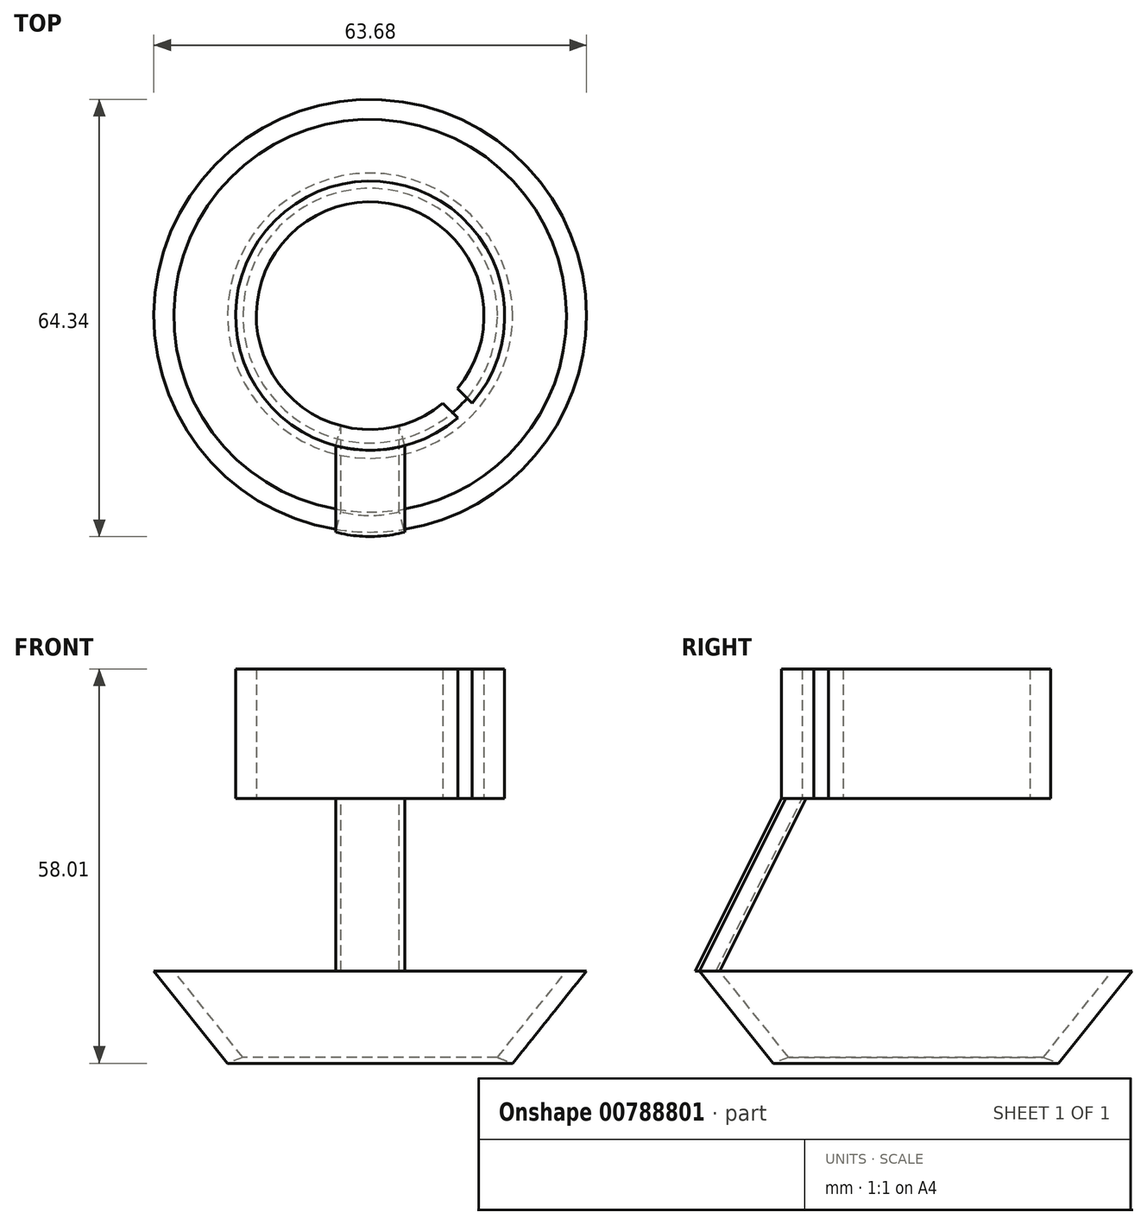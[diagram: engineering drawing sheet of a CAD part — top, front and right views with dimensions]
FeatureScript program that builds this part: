
annotation { "Feature Type Name" : "Feature", "Feature Type Description" : "" }
export const myFeature = defineFeature(function(context is Context, id is Id, definition is map)
    precondition{}
    {
        {
            var Q0;
            Q0=qCreatedBy(makeId("Top.planeOp"),FACE);
            var sketch = newSketch(context, id + "F0", { "sketchPlane" : qUnion([Q0])});
            skArc(sketch, "E0", {"start": v(12.87, -10.72) * mm, "mid": v(-11.84, 11.84) * mm, "end": v(10.72, -12.87) * mm});
            skArc(sketch, "E1.0", {"start": v(15.04, -12.88) * mm, "mid": v(-14, 14) * mm, "end": v(12.88, -15.04) * mm});
            skLineSegment(sketch, "E2", {"start": v(0, 0) * mm, "end": v(19.8, 0) * mm, "construction": true});
            skLineSegment(sketch, "E3", {"start": v(0, 0) * mm, "end": v(14.47, -14.47) * mm, "construction": true});
            skLineSegment(sketch, "E4.0", {"start": v(10.72, -12.87) * mm, "end": v(12.88, -15.04) * mm});
            skLineSegment(sketch, "E5.trimOffspring", {"start": v(12.87, -10.72) * mm, "end": v(15.04, -12.88) * mm});
            skSolve(sketch);
        }
        {
            var Q0;
            Q0=qSketchRegion(id+"F0",true);
            extrude(context, id + "F1", {"entities" : qUnion([Q0]), "depth" : 19.05 * mm, "offsetDistance" : 25.4 * mm});
        }
        {
            var Q0;
            Q0=makeQuery(id+"F1.opExtrude","CAP_FACE",FACE,{"disambiguationData":[OSD([sQuery(id+"F0.wireOp",EDGE,"E0"),sQuery(id+"F0.wireOp",EDGE,"E1.0")])],"isStart":true});
            var sketch = newSketch(context, id + "F2", { "sketchPlane" : qUnion([Q0])});
            skLineSegment(sketch, "E6", {"start": v(0, 0) * mm, "end": v(0, 22.55) * mm, "construction": true});
            skLineSegment(sketch, "E7", {"start": v(0, 22.55) * mm, "end": v(5.08, 22.55) * mm, "construction": true});
            skLineSegment(sketch, "E8", {"start": v(0, 22.55) * mm, "end": v(-5.08, 22.55) * mm, "construction": true});
            skLineSegment(sketch, "E9", {"start": v(-5.08, 22.55) * mm, "end": v(-5.08, 15.96) * mm, "construction": true});
            skLineSegment(sketch, "E10", {"start": v(5.08, 22.55) * mm, "end": v(5.08, 15.96) * mm, "construction": true});
            skLineSegment(sketch, "E11", {"start": v(-5.08, 19.14) * mm, "end": v(-4.3, 16.2) * mm});
            skLineSegment(sketch, "E12", {"start": v(5.08, 19.14) * mm, "end": v(4.3, 16.2) * mm});
            skArc(sketch, "E13.0", {"start": v(5.08, 19.14) * mm, "mid": v(0, -19.8) * mm, "end": v(-5.08, 19.14) * mm});
            skArc(sketch, "E14.0", {"start": v(5.08, 15.96) * mm, "mid": v(0, -16.75) * mm, "end": v(-5.08, 15.96) * mm});
            skPoint(sketch, "E15", {"position": v(-19.8, 0) * mm});
            skPoint(sketch, "E16", {"position": v(0, 19.8) * mm});
            skSolve(sketch);
        }
        {
            var Q0;
            Q0=qCreatedBy(makeId("Right.planeOp"),FACE);
            var sketch = newSketch(context, id + "F3", { "sketchPlane" : qUnion([Q0])});
            skPoint(sketch, "E17.0", {"position": v(-19.8, 0) * mm});
            skLineSegment(sketch, "E18", {"start": v(-19.8, 0) * mm, "end": v(-32.5, 0) * mm, "construction": true});
            skLineSegment(sketch, "E19", {"start": v(-32.5, 0) * mm, "end": v(-32.5, -25.4) * mm, "construction": true});
            skLineSegment(sketch, "E20", {"start": v(-32.5, -25.4) * mm, "end": v(-19.8, 0) * mm});
            skSolve(sketch);
        }
        {
            var Q0;
            {var subQ0=sQuery(id+"F2.wireOp",EDGE,"E11");Q0=makeQuery(id+"F2.imprint","IMPRINT",FACE,{"disambiguationData":[TD([[makeQuery(id+"F2.imprint","IMPRINT",EDGE,{"derivedFrom":subQ0}),1.0]])]});}
            var Q1;
            Q1=sQuery(id+"F3.wireOp",EDGE,"E20");
            sweep(context, id + "F4", {"operationType" : NewBodyOperationType.ADD, "profiles" : qUnion([Q0]), "path" : qUnion([Q1])});
        }
        {
            var Q0;
            Q0=qCreatedBy(makeId("Right.planeOp"),FACE);
            var sketch = newSketch(context, id + "F5", { "sketchPlane" : qUnion([Q0])});
            skLineSegment(sketch, "E21", {"start": v(0, -13.55) * mm, "end": v(0, 29.8) * mm});
            skSolve(sketch);
        }
        {
            var Q0;
            Q0=makeQuery(id+"F4.opSweep","CAP_FACE",FACE,{"disambiguationData":[OSD([sQuery(id+"F2.wireOp",EDGE,"E11"),sQuery(id+"F2.wireOp",EDGE,"E12"),sQuery(id+"F2.wireOp",EDGE,"E13.0"),sQuery(id+"F2.wireOp",EDGE,"E14.0"),sQuery(id+"F3.wireOp",VERTEX,"E20.start")])],"isStart":false});
            var sketch = newSketch(context, id + "F6", { "sketchPlane" : qUnion([Q0])});
            skPoint(sketch, "E22", {"position": v(5.08, 31.84) * mm});
            skPoint(sketch, "E23", {"position": v(4.3, 28.9) * mm});
            skSolve(sketch);
        }
        {
            var Q0;
            Q0=qCreatedBy(makeId("Right.planeOp"),FACE);
            var sketch = newSketch(context, id + "F7", { "sketchPlane" : qUnion([Q0])});
            skPoint(sketch, "E24.0", {"position": v(-31.84, -25.4) * mm});
            skPoint(sketch, "E25.0", {"position": v(-28.9, -25.4) * mm});
            skLineSegment(sketch, "E26", {"start": v(-28.9, -25.4) * mm, "end": v(-18.73, -25.4) * mm, "construction": true});
            skLineSegment(sketch, "E27", {"start": v(-18.73, -25.4) * mm, "end": v(-18.73, -38.1) * mm, "construction": true});
            skLineSegment(sketch, "E28", {"start": v(-28.9, -25.4) * mm, "end": v(-18.73, -38.1) * mm});
            skLineSegment(sketch, "E29", {"start": v(-31.84, -25.4) * mm, "end": v(-28.9, -25.4) * mm});
            skLineSegment(sketch, "E30", {"start": v(-31.84, -25.4) * mm, "end": v(-20.99, -38.96) * mm});
            skLineSegment(sketch, "E31", {"start": v(-20.99, -38.96) * mm, "end": v(-18.73, -38.1) * mm});
            skLineSegment(sketch, "E32", {"start": v(0, 0) * mm, "end": v(0, -32.23) * mm});
            skSolve(sketch);
        }
        {
            var Q0;
            Q0=qSketchRegion(id+"F7",true);
            var Q1;
            Q1=sQuery(id+"F7.wireOp",EDGE,"E32");
            revolve(context, id + "F8", {"operationType" : NewBodyOperationType.ADD, "surfaceOperationType" : NewSurfaceOperationType.NEW, "entities" : qUnion([Q0]), "axis" : qUnion([Q1]), "revolveType" : RevolveType.FULL});
        }
    });
